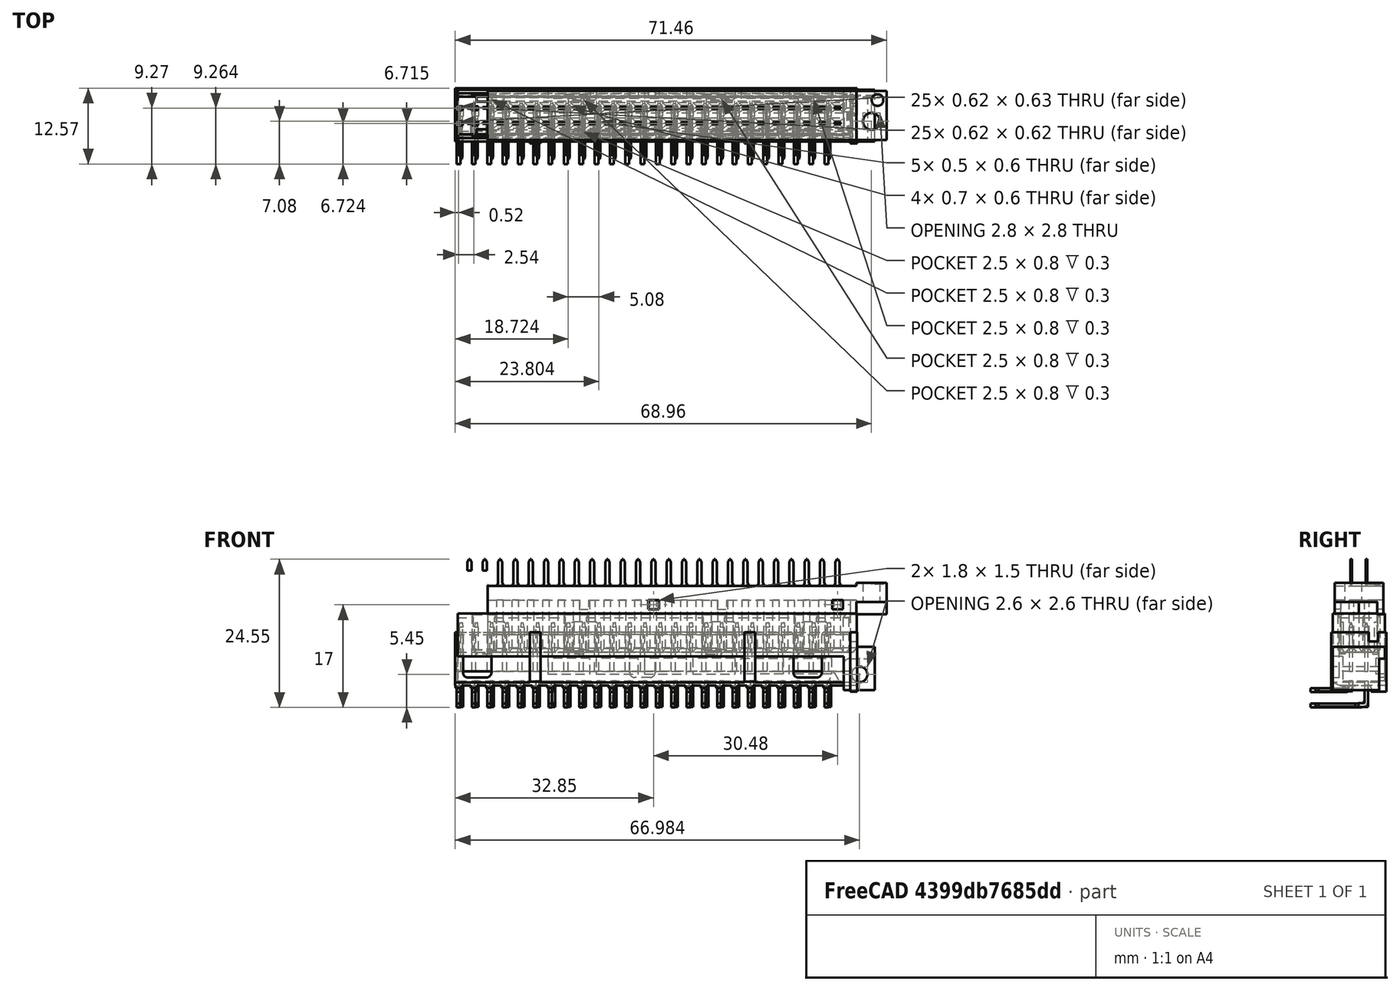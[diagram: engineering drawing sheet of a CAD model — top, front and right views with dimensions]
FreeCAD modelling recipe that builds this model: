
FCSTD DOCUMENT  (FreeCAD 0.21R33771 (Git))
Label: PCN10x_test
License: All rights reserved
LicenseURL: http://en.wikipedia.org/wiki/All_rights_reserved
objects: Part::Feature×3, Part::Box×3, Part::Cut×3, App::MeasureDistance×3
note: 9 computed .brp shape members not serialized (recipe doc carries the construction recipe); baked Part::Feature solids carry a one-line shape summary decoded from their .brp

FEATURE [Part::Feature] Part__Feature  label="PCN10A-50P-2.54DS"
  Placement = pos=(53.3739,-4.26558,-11.3) rot=(0,0,-1;4.71239rad)
  shape: bbox 76.22 x 11.5 x 15.48 mm, 1514 faces (baked)
FEATURE [Part::Feature] Part__Feature001  label="C-1-103310-0"
  Placement = pos=(0,0,-1.6) rot=(0,0,1;0rad)
  shape: bbox 71.12 x 12.57 x 12.45 mm, 812 faces (baked)
FEATURE [Part::Box] Box  label="Cube"
  AttacherType = Attacher::AttachEngine3D
  Height = 21
  Length = 13
  Placement = pos=(-44,-9,-16) rot=(0,0,1;0rad)
  Width = 17
FEATURE [Part::Cut] Cut
  Base = -> Part__Feature
  Placement = pos=(0,0,-3) rot=(0,0,1;0rad)
  Tool = -> Box
FEATURE [Part::Box] Box001  label="Cube001"
  AttacherType = Attacher::AttachEngine3D
  Height = 21
  Length = 13
  Placement = pos=(-44,-9,-16) rot=(0,0,1;0rad)
  Width = 17
FEATURE [Part::Cut] Cut001
  Base = -> Part__Feature001
  Placement = pos=(-0.4,0,-3.1) rot=(0,0,1;0rad)
  Tool = -> Box001
FEATURE [Part::Feature] Part__Feature002  label="PCN10C-50S-2.54DSA"
  Placement = pos=(17.2,-4,6.3e-15) rot=(0,-1,0;3.14159rad)
  shape: bbox 77.22 x 8.1 x 15.4 mm, 1118 faces (baked)
FEATURE [Part::Box] Box002  label="Cube002"
  AttacherType = Attacher::AttachEngine3D
  Height = 21
  Length = 13
  Placement = pos=(-26,-9,2) rot=(0,-1,0;3.14159rad)
  Width = 17
FEATURE [Part::Cut] Cut002
  Base = -> Part__Feature002
  Placement = pos=(0,0,3.5) rot=(0,0,1;0rad)
  Tool = -> Box002
FEATURE [App::MeasureDistance] Distance  label="Distance: 6,10 mm"
  Distance = 6.09958
  P1 = (-31.4,1.57334,-8.077)
  P2 = (-31.1911,1.58115,-1.981)
FEATURE [App::MeasureDistance] Distance001  label="Distance: 7,98 mm"
  Distance = 7.97779
  P1 = (-26,-0.82,0.6)
  P2 = (-26,-0.82,-7.37779)
FEATURE [App::MeasureDistance] Distance002  label="Distance: 8,56 mm"
  Distance = 8.55819
  P1 = (-26,-0.364932,-7.94608)
  P2 = (-26,-0.82,0.6)
